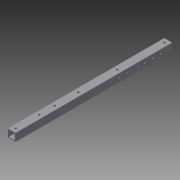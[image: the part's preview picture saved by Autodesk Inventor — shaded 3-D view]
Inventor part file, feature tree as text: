
AUTODESK INVENTOR PART (.ipt)
format: ipt  version: 2015 SP1 (Build 190203100, 203)  size: 160,256 bytes
history: native  units: in
note: dims shown in document units (in); Inventor stores cm internally (conversion verified against a paired STEP export)
features: sketch x7, hole x5, projected_geometry x3, extrude x2
ambient origin geometry x8: Origin, YZ Plane, XZ Plane, XY Plane, X Axis, Y Axis, Z Axis, Center Point
bodies: Solid1 (feature_tree)
feature tree (17):
  extrude  "Extrusion1"  Depth=1.0in
  sketch  "Sketch2"  dims[d2=0.75in d3=0.75in]
  hole  "Hole2"  [1 undecoded]
  hole  "Hole3"  [1 undecoded]
  hole  "Hole4"  [1 undecoded]
  extrude  "Extrusion2"  Depth=0.5in
  hole  "Hole6"  [1 undecoded]
  hole  "Hole7"  [1 undecoded]
  sketch  "Sketch1"  dims[d0=1.0in d1=1.0in]
  projected_geometry  "Projected Loop1"
  sketch  "Sketch3"  dims[d4=0.125in d5=0.125in]
  sketch  "Sketch4"  dims[d6=12.0in d7=0.0in d8=0.5in]
  projected_geometry  "Projected Loop2"
  sketch  "Sketch5"  dims[d9=0.5in d10=0.5in]
  sketch  "Sketch6"  dims[d11=0.5in d19=0.5in]
  sketch  "Sketch7"  dims[d20=0.5in d21=0.5in d22=1.5in d23=3.5in d24=2.5in d25=0.1562in d26=0.75in d27=0.375in d28=0.25in d29=0.5635in d30=1.0in d31=0.8108in d32=0.5in d33=5.5in d34=0.25in d35=0.75in d36=0.375in d37=0.25in d38=0.5635in d39=1.0in d40=0.8108in d41=5.25in d42=7.75in d43=6.25in d44=0.5in d45=0.5in d46=0.5in d47=0.1562in d48=0.75in d49=0.375in d50=0.25in d51=0.5635in d52=1.0in d53=0.8108in d54=8.0in d55=0.0in d56=0.5in d57=0.5in d65=3.5in d66=0.5in d67=0.25in d68=0.75in d69=0.375in d70=0.25in d71=0.5635in d72=1.0in d73=0.8108in d74=0.5in d75=0.5in d76=4.5in d77=7.5in d78=0.25in d79=0.75in d80=0.375in d81=0.25in d82=0.5635in d83=1.0in d84=0.8108in]
  projected_geometry  "Projected Loop3"
note: 5 required parameter values undecoded (feature->parameter linkage not recoverable at this tier; creation-order binding heuristic only, values carry confidence <= 0.55)
